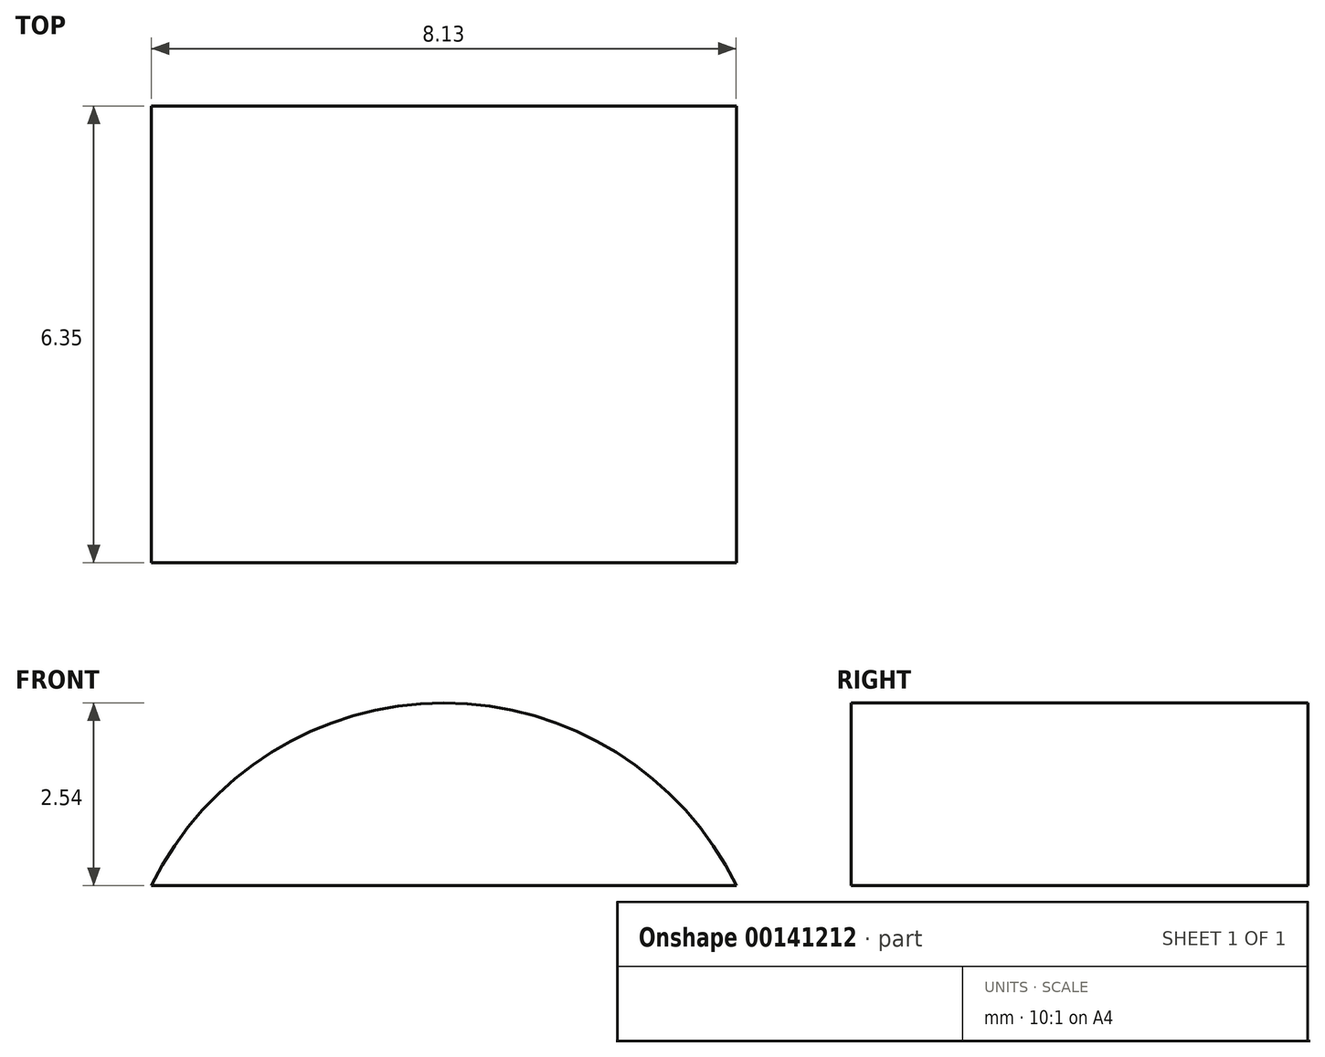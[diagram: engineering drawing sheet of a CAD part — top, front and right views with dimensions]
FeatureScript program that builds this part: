
annotation { "Feature Type Name" : "Feature", "Feature Type Description" : "" }
export const myFeature = defineFeature(function(context is Context, id is Id, definition is map)
    precondition{}
    {
        {
            var Q0;
            Q0=qCreatedBy(makeId("Front.planeOp"),FACE);
            var sketch = newSketch(context, id + "F0", { "sketchPlane" : qUnion([Q0])});
            skLineSegment(sketch, "E0", {"start": v(0, 0) * mm, "end": v(8.13, 0) * mm});
            skArc(sketch, "E1", {"start": v(8.13, 0) * mm, "mid": v(4.07, 2.54) * mm, "end": v(0, 0) * mm});
            skSolve(sketch);
        }
        {
            var Q0;
            Q0=makeQuery(id+"F0.imprint","IMPRINT",FACE,{"disambiguationData":[TD([[makeQuery(id+"F0.imprint","IMPRINT",EDGE,{"derivedFrom":sQuery(id+"F0.wireOp",EDGE,"E0")}),1.0]])]});
            extrude(context, id + "F1", {"entities" : qUnion([Q0]), "depth" : 6.35 * mm});
        }
    });
